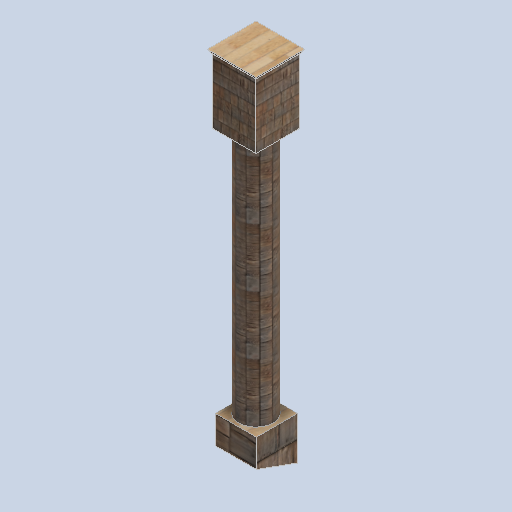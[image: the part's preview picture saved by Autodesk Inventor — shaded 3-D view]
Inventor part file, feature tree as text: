
AUTODESK INVENTOR PART (.ipt)
format: ipt  version: 2024.2 (Build 282272000, 272)  size: 173,056 bytes
history: native  units: in
note: dims shown in document units (in); Inventor stores cm internally (conversion verified against a paired STEP export)
features: sketch x5, other x3, plane x1
ambient origin geometry x8: Origin, YZ Plane, XZ Plane, XY Plane, X Axis, Y Axis, Z Axis, Center Point
bodies: Solid1 (feature_tree)
feature tree (9):
  other  "side_pillar_01_MIR.ipt"
  other  "Solid1::side_pillar_01_MIR.ipt"
  other  "TaggingFeature1"
  sketch  "Sketch1"  dims[d0=0.3937in]
  sketch  "Sketch2"
  sketch  "Sketch3"
  sketch  "Sketch4"
  sketch  "Sketch5"
  plane  "Work Plane3"
